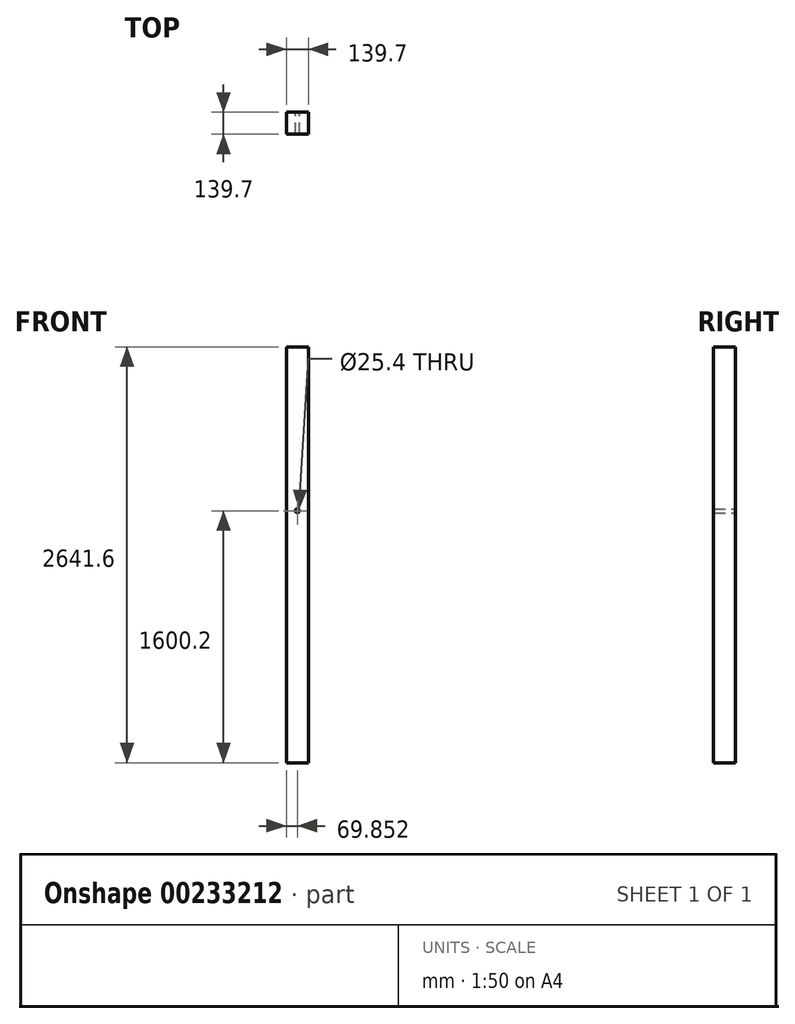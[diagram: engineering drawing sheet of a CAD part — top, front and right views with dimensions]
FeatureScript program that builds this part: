
annotation { "Feature Type Name" : "Feature", "Feature Type Description" : "" }
export const myFeature = defineFeature(function(context is Context, id is Id, definition is map)
    precondition{}
    {
        {
            var Q0;
            Q0=qCreatedBy(makeId("Front.planeOp"),FACE);
            var sketch = newSketch(context, id + "F0", { "sketchPlane" : qUnion([Q0])});
            skLineSegment(sketch, "E0.bottom", {"start": v(-55.56, 2618.96) * mm, "end": v(84.14, 2618.96) * mm});
            skLineSegment(sketch, "E0.top", {"start": v(-55.56, -22.64) * mm, "end": v(84.14, -22.64) * mm});
            skLineSegment(sketch, "E0.left", {"start": v(-55.56, 2618.96) * mm, "end": v(-55.56, -22.64) * mm});
            skLineSegment(sketch, "E0.right", {"start": v(84.14, 2618.96) * mm, "end": v(84.14, -22.64) * mm});
            skCircle(sketch, "E1", {"center": v(14.3, 1577.56) * mm, "radius": 12.7 * mm});
            skSolve(sketch);
        }
        {
            var Q0;
            Q0 = qSketchRegion(id + "F0", true);
            extrude(context, id + "F1", {"entities" : qUnion([Q0]), "depth" : 139.7 * mm});
        }
    });
